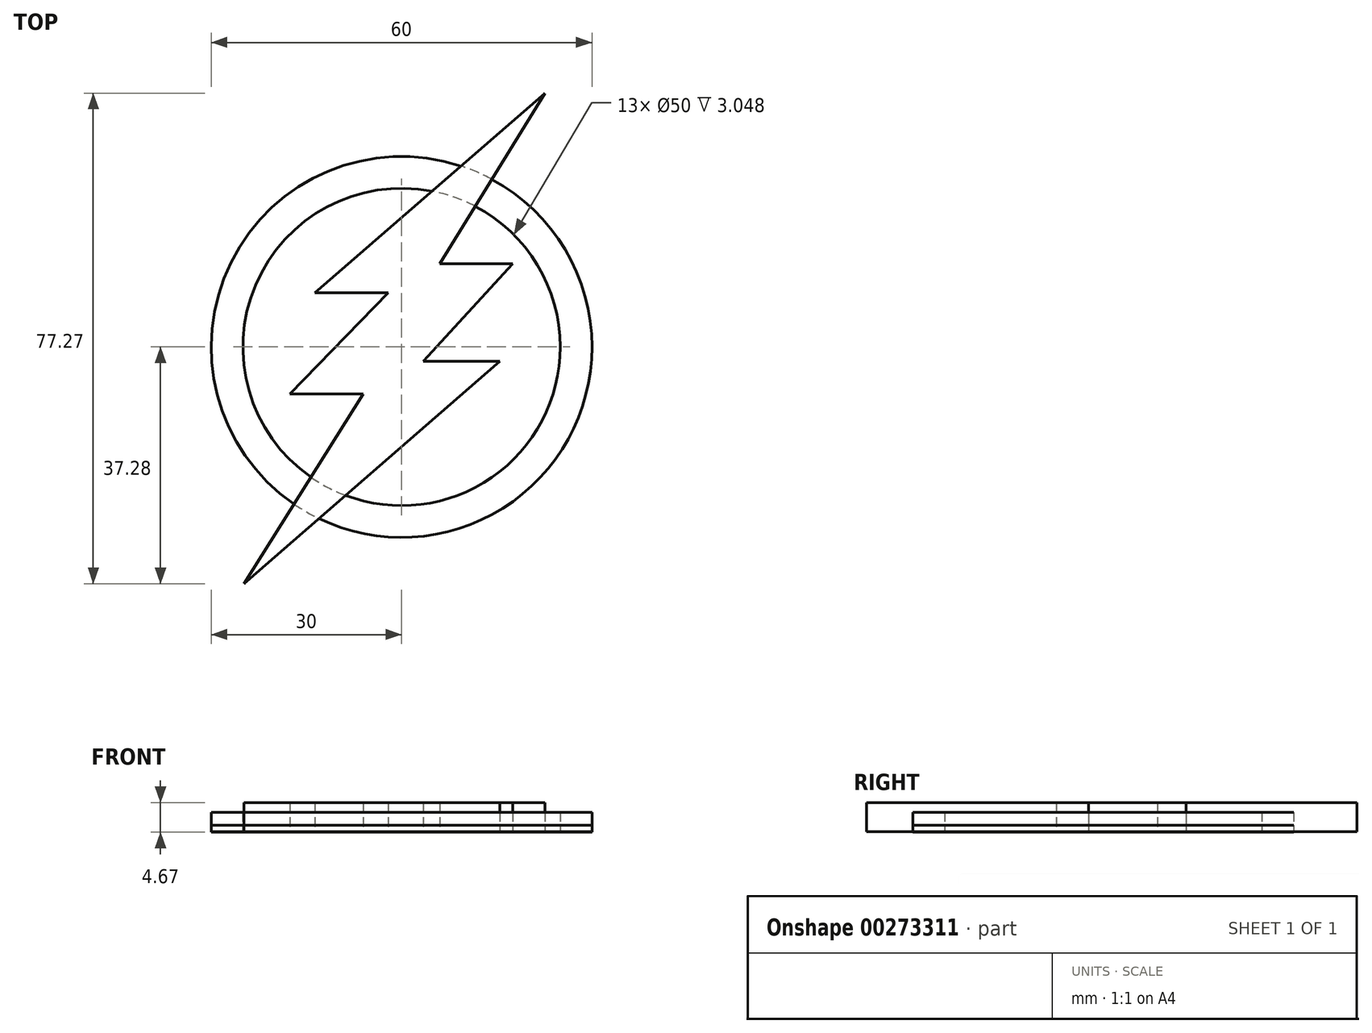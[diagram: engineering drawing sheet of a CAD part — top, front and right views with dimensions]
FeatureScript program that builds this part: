
annotation { "Feature Type Name" : "Feature", "Feature Type Description" : "" }
export const myFeature = defineFeature(function(context is Context, id is Id, definition is map)
    precondition{}
    {
        {
            var Q0;
            Q0=qCreatedBy(makeId("Top.planeOp"),FACE);
            var sketch = newSketch(context, id + "F0", { "sketchPlane" : qUnion([Q0])});
            skCircle(sketch, "E0", {"center": v(0, 0) * mm, "radius": 25 * mm});
            skSolve(sketch);
        }
        {
            var Q0;
            Q0=makeQuery(id+"F0.imprint","IMPRINT",FACE,{"disambiguationData":[TD([[makeQuery(id+"F0.imprint","IMPRINT",EDGE,{"derivedFrom":sQuery(id+"F0.wireOp",EDGE,"E0")}),1.0]])]});
            var sketch = newSketch(context, id + "F1", { "sketchPlane" : qUnion([Q0])});
            skCircle(sketch, "E1", {"center": v(0, 0) * mm, "radius": 30 * mm});
            skSolve(sketch);
        }
        {
            var Q0;
            Q0=qCreatedBy(makeId("Top.planeOp"),FACE);
            var sketch = newSketch(context, id + "F2", { "sketchPlane" : qUnion([Q0])});
            skLineSegment(sketch, "E2", {"start": v(22.6, 40) * mm, "end": v(-13.65, 8.53) * mm});
            skLineSegment(sketch, "E3", {"start": v(-13.65, 8.53) * mm, "end": v(-2.09, 8.53) * mm});
            skLineSegment(sketch, "E4", {"start": v(-2.09, 8.53) * mm, "end": v(-17.62, -7.4) * mm});
            skLineSegment(sketch, "E5", {"start": v(-17.62, -7.4) * mm, "end": v(-6.03, -7.4) * mm});
            skLineSegment(sketch, "E6", {"start": v(-6.03, -7.4) * mm, "end": v(-24.87, -37.28) * mm});
            skLineSegment(sketch, "E7", {"start": v(-24.87, -37.28) * mm, "end": v(15.46, -2.28) * mm});
            skLineSegment(sketch, "E8", {"start": v(15.46, -2.28) * mm, "end": v(3.41, -2.28) * mm});
            skLineSegment(sketch, "E9", {"start": v(3.41, -2.28) * mm, "end": v(17.5, 13.08) * mm});
            skLineSegment(sketch, "E10", {"start": v(17.5, 13.08) * mm, "end": v(6.04, 13.08) * mm});
            skLineSegment(sketch, "E11", {"start": v(6.04, 13.08) * mm, "end": v(22.6, 40) * mm});
            skSolve(sketch);
        }
        {
            var Q0;
            Q0=sQuery(id+"F1.wireOp",EDGE,"E1");
            extrude(context, id + "F3", {"bodyType" : ToolBodyType.SURFACE, "surfaceEntities" : qUnion([Q0]), "depth" : 3 * mm});
        }
        {
            var Q0;
            Q0=sQuery(id+"F0.wireOp",EDGE,"E0");
            extrude(context, id + "F4", {"bodyType" : ToolBodyType.SURFACE, "surfaceEntities" : qUnion([Q0]), "depth" : 3 * mm});
        }
        {
            var Q0;
            Q0=makeQuery(id+"F1.imprint","IMPRINT",FACE,{"disambiguationData":[TD([[makeQuery(id+"F1.imprint","IMPRINT",EDGE,{"derivedFrom":makeQuery(id+"F0.imprint","IMPRINT",EDGE,{"derivedFrom":sQuery(id+"F0.wireOp",EDGE,"E0")})}),1.0]])]});
            var Q1;
            Q1=makeQuery(id+"F1.imprint","IMPRINT",FACE,{"disambiguationData":[TD([[makeQuery(id+"F1.imprint","IMPRINT",EDGE,{"derivedFrom":sQuery(id+"F1.wireOp",EDGE,"E1")}),1.0]])]});
            extrude(context, id + "F5", {"entities" : qUnion([Q0, Q1]), "depth" : 1 * mm});
        }
        {
            var Q0;
            Q0=makeQuery(id+"F1.imprint","IMPRINT",FACE,{"disambiguationData":[TD([[makeQuery(id+"F1.imprint","IMPRINT",EDGE,{"derivedFrom":sQuery(id+"F1.wireOp",EDGE,"E1")}),1.0]])]});
            var Q1;
            Q1=makeQuery(id+"F1.imprint","IMPRINT",FACE,{"disambiguationData":[TD([[makeQuery(id+"F1.imprint","IMPRINT",EDGE,{"derivedFrom":makeQuery(id+"F0.imprint","IMPRINT",EDGE,{"derivedFrom":sQuery(id+"F0.wireOp",EDGE,"E0")})}),1.0]])]});
            extrude(context, id + "F6", {"entities" : qUnion([Q0, Q1]), "oppositeDirection" : true, "depth" : 0.1 * mm});
        }
        {
            var Q0;
            Q0=makeQuery(id+"F1.imprint","IMPRINT",FACE,{"disambiguationData":[TD([[makeQuery(id+"F1.imprint","IMPRINT",EDGE,{"derivedFrom":sQuery(id+"F1.wireOp",EDGE,"E1")}),1.0]])]});
            extrude(context, id + "F7", {"entities" : qUnion([Q0]), "depth" : 3.05 * mm});
        }
        {
            var Q0;
            Q0 = qSketchRegion(id + "F2", true);
            extrude(context, id + "F8", {"entities" : qUnion([Q0]), "depth" : 4.57 * mm});
        }
    });
